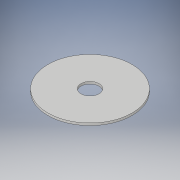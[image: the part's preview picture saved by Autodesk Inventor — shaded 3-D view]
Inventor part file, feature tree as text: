
AUTODESK INVENTOR PART (.ipt)
format: ipt  version: 2017 (Build 210142000, 142)  size: 94,208 bytes
history: native  units: in
note: dims shown in document units (in); Inventor stores cm internally (conversion verified against a paired STEP export)
features: extrude x1, sketch x1
ambient origin geometry x8: Origin, YZ Plane, XZ Plane, XY Plane, X Axis, Y Axis, Z Axis, Center Point
bodies: Solid1 (feature_tree)
feature tree (2):
  extrude  "Extrusion1"  Depth=0.05in
  sketch  "Sketch1"  dims[d0=1.9in d1=0.405in d2=0.05in d3=0.0in]
